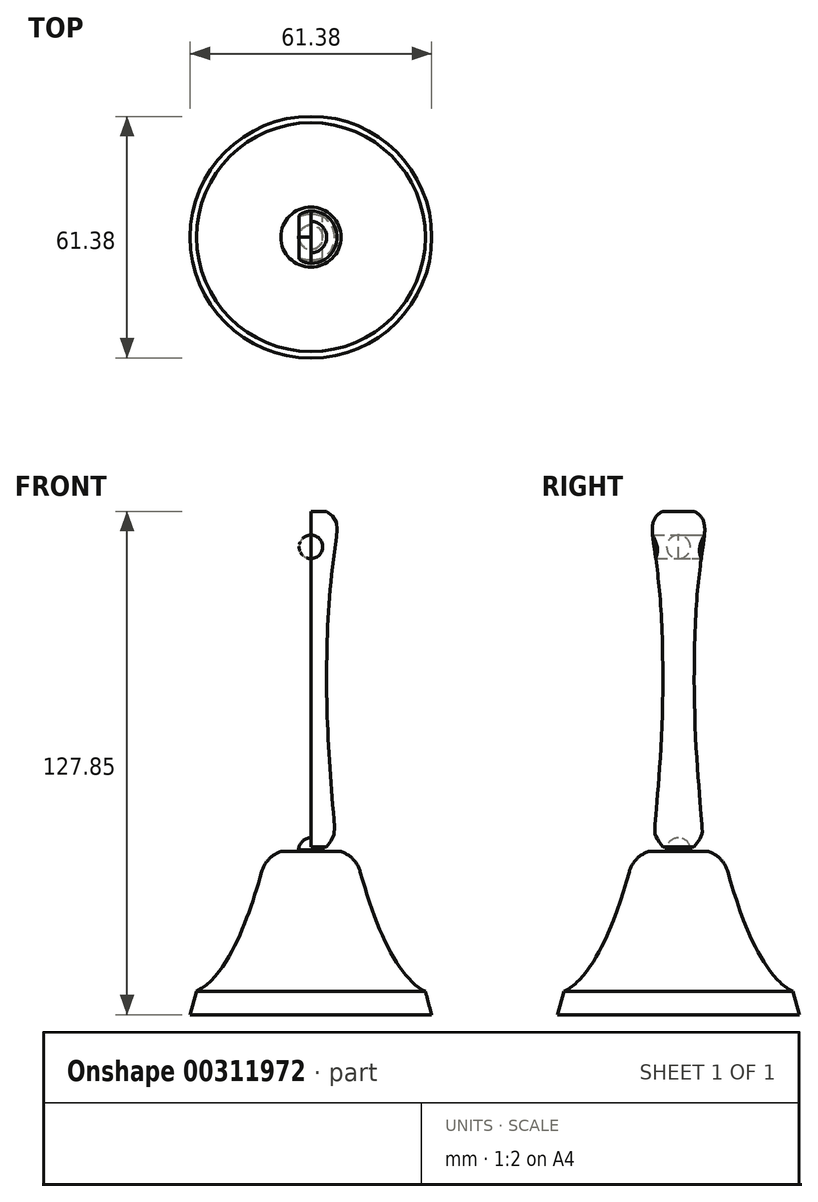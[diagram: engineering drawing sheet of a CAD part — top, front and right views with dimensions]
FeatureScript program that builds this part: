
annotation { "Feature Type Name" : "Feature", "Feature Type Description" : "" }
export const myFeature = defineFeature(function(context is Context, id is Id, definition is map)
    precondition{}
    {
        {
            var Q0;
            Q0=qCreatedBy(makeId("Front.planeOp"),FACE);
            var sketch = newSketch(context, id + "F0", { "sketchPlane" : qUnion([Q0])});
            skLineSegment(sketch, "E0", {"start": v(0, 56.82) * mm, "end": v(-2.66, 56.82) * mm});
            skFitSpline(sketch, "E1", {"points": [v(-2.66, 56.82) * mm, v(-4.14, 50.82) * mm, v(-2.66, 28.41) * mm], "startDerivative": vector(-19.91, -8.94) * mm, "endDerivative": vector(0, -51.99) * mm});
            skLineSegment(sketch, "E2", {"start": v(0, 0) * mm, "end": v(0, 28.41) * mm, "construction": true});
            skLineSegment(sketch, "E3", {"start": v(0, 28.41) * mm, "end": v(0, 56.82) * mm, "construction": true});
            skLineSegment(sketch, "E4", {"start": v(-2.66, 28.41) * mm, "end": v(0, 28.41) * mm, "construction": true});
            skFitSpline(sketch, "E5", {"points": [v(-2.66, 28.41) * mm, v(-3.99, 3.35) * mm, v(-2.66, 0) * mm], "startDerivative": vector(0, -47.03) * mm, "endDerivative": vector(14.93, -19.3) * mm});
            skLineSegment(sketch, "E6", {"start": v(-2.66, 0) * mm, "end": v(0, 0) * mm});
            skLineSegment(sketch, "E7", {"start": v(-2.66, 39.78) * mm, "end": v(-2.66, 28.41) * mm, "construction": true});
            skLineSegment(sketch, "E8", {"start": v(-2.66, 17.04) * mm, "end": v(-2.66, 28.41) * mm, "construction": true});
            skLineSegment(sketch, "E9", {"start": v(0, 0) * mm, "end": v(0, -28.41) * mm, "construction": true});
            skLineSegment(sketch, "E10", {"start": v(0, -28.41) * mm, "end": v(-20.46, -28.41) * mm});
            skLineSegment(sketch, "E11", {"start": v(-20.46, -28.41) * mm, "end": v(-19.38, -24.5) * mm});
            skFitSpline(sketch, "E12", {"points": [v(-19.38, -24.5) * mm, v(-7.66, -1.63) * mm], "startDerivative": vector(14.57, 7.44) * mm, "endDerivative": vector(9.06, 35.28) * mm});
            skLineSegment(sketch, "E13", {"start": v(-5.08, -0.8) * mm, "end": v(-2.66, 0) * mm, "construction": true});
            skArc(sketch, "E14.filletArc", {"start": v(-5.08, -0.8) * mm, "mid": v(-7.14, -2.09) * mm, "end": v(-8.35, -4.2) * mm});
            skLineSegment(sketch, "E15", {"start": v(0, 0) * mm, "end": v(0, 56.82) * mm});
            skLineSegment(sketch, "E16", {"start": v(0, 0) * mm, "end": v(0, -28.41) * mm});
            skLineSegment(sketch, "E17", {"start": v(0, 56.82) * mm, "end": v(0, 50.82) * mm});
            skCircle(sketch, "E18", {"center": v(0, 50.82) * mm, "radius": 2 * mm});
            skLineSegment(sketch, "E19", {"start": v(-5.08, -0.8) * mm, "end": v(0, -0.8) * mm});
            skSolve(sketch);
        }
        {
            var Q0;
            Q0=qCreatedBy(makeId("Front.planeOp"),FACE);
            var sketch = newSketch(context, id + "F1", { "sketchPlane" : qUnion([Q0])});
            skPoint(sketch, "E20.0", {"position": v(0, -0.8) * mm});
            skArc(sketch, "E21", {"start": v(0, 2.32) * mm, "mid": v(-2.2, 1.4) * mm, "end": v(-3.1, -0.8) * mm});
            skLineSegment(sketch, "E22", {"start": v(-3.1, -0.8) * mm, "end": v(0, -0.8) * mm});
            skLineSegment(sketch, "E23", {"start": v(0, -0.8) * mm, "end": v(0, 2.32) * mm});
            skSolve(sketch);
        }
        {
            var Q0;
            Q0=makeQuery(id+"F0.imprint","IMPRINT",FACE,{"disambiguationData":[TD([[makeQuery(id+"F0.imprint","IMPRINT",EDGE,{"derivedFrom":sQuery(id+"F0.wireOp",EDGE,"E0")}),1.0]])]});
            var Q1;
            Q1=sQuery(id+"F0.wireOp",EDGE,"E15");
            revolve(context, id + "F2", {"entities" : qUnion([Q0]), "axis" : qUnion([Q1]), "revolveType" : RevolveType.FULL});
        }
        {
            var Q0;
            {var subQ1=sQuery(id+"F0.wireOp",EDGE,"E10");Q0=makeQuery(id+"F0.imprint","IMPRINT",FACE,{"disambiguationData":[TD([[makeQuery(id+"F0.imprint","IMPRINT",EDGE,{"derivedFrom":subQ1}),-1.0]])]});}
            var Q1;
            Q1=sQuery(id+"F0.wireOp",EDGE,"E16");
            revolve(context, id + "F3", {"entities" : qUnion([Q0]), "axis" : qUnion([Q1]), "revolveType" : RevolveType.FULL});
        }
        {
            var Q0;
            {var subQ0=sQuery(id+"F0.wireOp",EDGE,"E17");var subQ1=sQuery(id+"F0.wireOp",EDGE,"E15");var subQ2=makeQuery(id+"F0.imprint","INTERSECT",VERTEX,{"derivedFrom":[subQ1,subQ0]});Q0=makeQuery(id+"F0.imprint","IMPRINT",FACE,{"disambiguationData":[TD([[makeQuery(id+"F0.imprint","IMPRINT",EDGE,{"disambiguationData":[TD([[subQ2,1.0]])],"derivedFrom":subQ1}),1.0]])]});}
            var Q1;
            {var subQ0=sQuery(id+"F0.wireOp",EDGE,"E17");var subQ1=sQuery(id+"F0.wireOp",EDGE,"E15");var subQ2=makeQuery(id+"F0.imprint","INTERSECT",VERTEX,{"derivedFrom":[subQ1,subQ0]});Q1=makeQuery(id+"F0.imprint","IMPRINT",FACE,{"disambiguationData":[TD([[makeQuery(id+"F0.imprint","IMPRINT",EDGE,{"disambiguationData":[TD([[subQ2,1.0]])],"derivedFrom":subQ1}),-1.0]])]});}
            extrude(context, id + "F4", {"entities" : qUnion([Q0, Q1]), "operationType" : NewBodyOperationType.REMOVE, "endBound" : BoundingType.THROUGH_ALL, "depth" : 25 * mm, "offsetDistance" : 25 * mm, "hasSecondDirection" : true, "secondDirectionBound" : SecondDirectionBoundingType.THROUGH_ALL, "secondDirectionOppositeDirection" : true, "secondDirectionDepth" : 25 * mm});
        }
        {
            var Q0;
            Q0=makeQuery(id+"F3.opRevolve","SWEPT_BODY",BODY,{"disambiguationData":[OSD([sQuery(id+"F0.wireOp",EDGE,"E6"),sQuery(id+"F0.wireOp",EDGE,"E10"),sQuery(id+"F0.wireOp",EDGE,"E11"),sQuery(id+"F0.wireOp",EDGE,"E12"),sQuery(id+"F0.wireOp",EDGE,"E13"),sQuery(id+"F0.wireOp",EDGE,"E14.filletArc"),sQuery(id+"F0.wireOp",EDGE,"E16")])]});
            var Q1;
            Q1=makeQuery(id+"F2.opRevolve","SWEPT_BODY",BODY,{"disambiguationData":[OSD([sQuery(id+"F0.wireOp",EDGE,"E0"),sQuery(id+"F0.wireOp",EDGE,"E1"),sQuery(id+"F0.wireOp",EDGE,"E5"),sQuery(id+"F0.wireOp",EDGE,"E6"),sQuery(id+"F0.wireOp",EDGE,"E15")])]});
            var Q2;
            Q2=sQuery(id+"F0.wireOp",VERTEX,"E16.start");
            transform(context, id + "F5", {"entities" : qUnion([Q0, Q1]), "transformType" : TransformType.SCALE_UNIFORMLY, "scale" : 1.5, "scalePoint" : qUnion([Q2]), "makeCopy" : false});
        }
        {
            var Q0;
            Q0=makeQuery(id+"F1.imprint","IMPRINT",FACE,{"disambiguationData":[TD([[makeQuery(id+"F1.imprint","IMPRINT",EDGE,{"derivedFrom":sQuery(id+"F1.wireOp",EDGE,"E21")}),1.0]])]});
            var Q1;
            Q1=sQuery(id+"F0.wireOp",EDGE,"E16");
            revolve(context, id + "F6", {"operationType" : NewBodyOperationType.ADD, "entities" : qUnion([Q0]), "axis" : qUnion([Q1]), "revolveType" : RevolveType.FULL});
        }
        {
            var Q0;
            Q0=makeQuery(id+"F3.opRevolve","SWEPT_BODY",BODY,{"disambiguationData":[OSD([sQuery(id+"F0.wireOp",EDGE,"E10"),sQuery(id+"F0.wireOp",EDGE,"E11"),sQuery(id+"F0.wireOp",EDGE,"E12"),sQuery(id+"F0.wireOp",EDGE,"E14.filletArc"),sQuery(id+"F0.wireOp",EDGE,"E16"),sQuery(id+"F0.wireOp",EDGE,"E19")])]});
            var Q1;
            Q1=makeQuery(id+"F2.opRevolve","SWEPT_BODY",BODY,{"disambiguationData":[OSD([sQuery(id+"F0.wireOp",EDGE,"E0"),sQuery(id+"F0.wireOp",EDGE,"E1"),sQuery(id+"F0.wireOp",EDGE,"E5"),sQuery(id+"F0.wireOp",EDGE,"E6"),sQuery(id+"F0.wireOp",EDGE,"E15"),sQuery(id+"F0.wireOp",EDGE,"E17"),sQuery(id+"F0.wireOp",EDGE,"E18")])]});
            booleanBodies(context, id + "F7", {"operationType" : BooleanOperationType.SUBTRACTION, "tools" : qUnion([Q0]), "targets" : qUnion([Q1]), "keepTools" : true});
        }
        {
            var Q0;
            Q0=makeQuery(id+"F2.opRevolve","SWEPT_BODY",BODY,{"disambiguationData":[OSD([sQuery(id+"F0.wireOp",EDGE,"E0"),sQuery(id+"F0.wireOp",EDGE,"E1"),sQuery(id+"F0.wireOp",EDGE,"E5"),sQuery(id+"F0.wireOp",EDGE,"E6"),sQuery(id+"F0.wireOp",EDGE,"E15"),sQuery(id+"F0.wireOp",EDGE,"E17"),sQuery(id+"F0.wireOp",EDGE,"E18")])]});
            var Q1;
            Q1=sQuery(id+"F0.wireOp",VERTEX,"E2.start");
            transform(context, id + "F8", {"entities" : qUnion([Q0]), "transformType" : TransformType.SCALE_UNIFORMLY, "scale" : 1, "scalePoint" : qUnion([Q1]), "makeCopy" : false});
        }
    });
